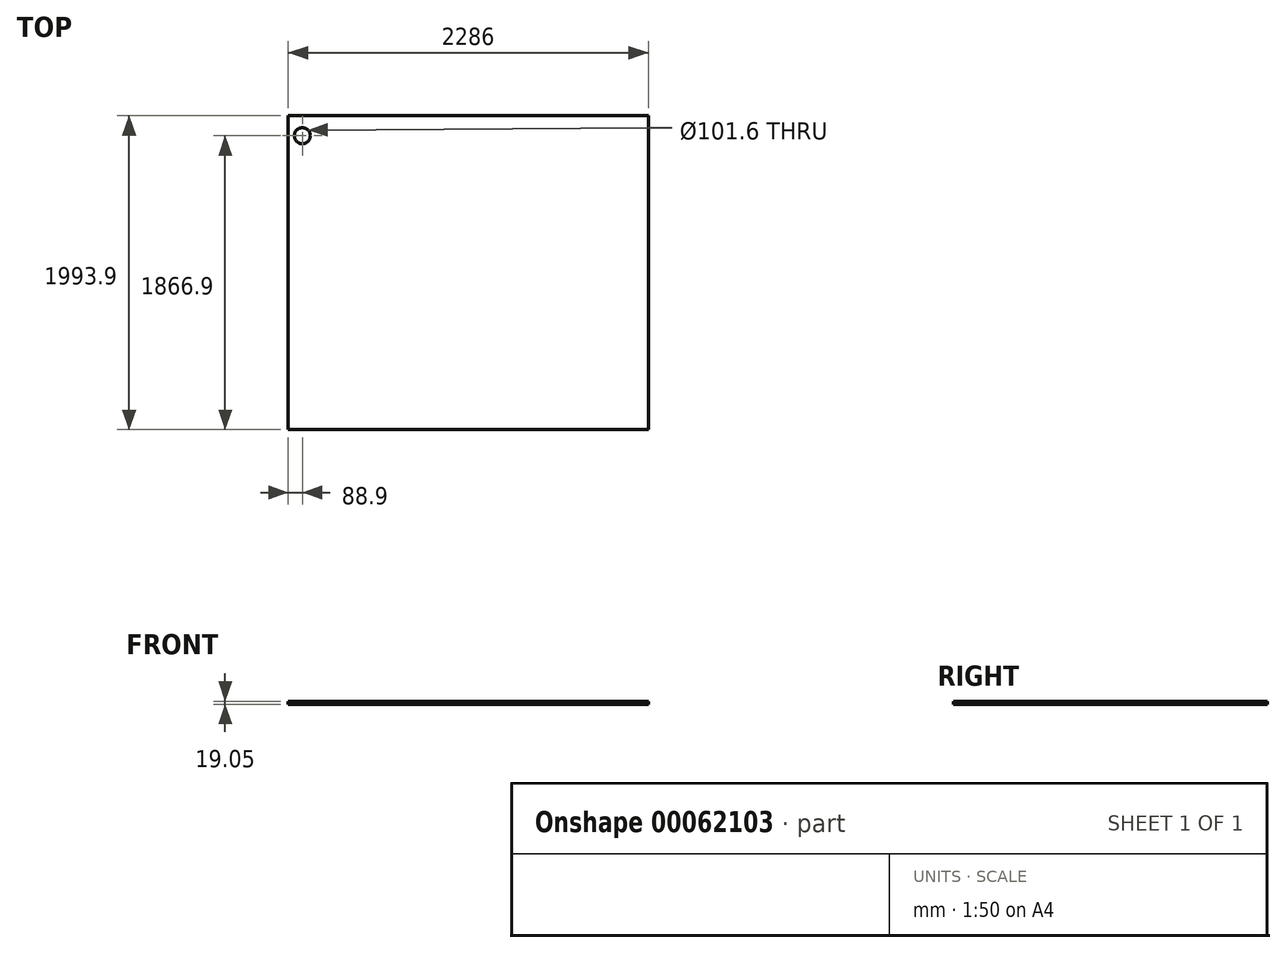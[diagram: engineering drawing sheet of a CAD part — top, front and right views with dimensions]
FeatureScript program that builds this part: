
annotation { "Feature Type Name" : "Feature", "Feature Type Description" : "" }
export const myFeature = defineFeature(function(context is Context, id is Id, definition is map)
    precondition{}
    {
        {
            var Q0;
            Q0=qCreatedBy(makeId("Top.planeOp"),FACE);
            var sketch = newSketch(context, id + "F0", { "sketchPlane" : qUnion([Q0])});
            skLineSegment(sketch, "E0", {"start": v(0, 0) * mm, "end": v(0, 985.96) * mm, "construction": true});
            skLineSegment(sketch, "E1", {"start": v(0, 0) * mm, "end": v(1088.04, 0) * mm, "construction": true});
            skLineSegment(sketch, "E2.bottom", {"start": v(-1143, 996.95) * mm, "end": v(1143, 996.95) * mm});
            skLineSegment(sketch, "E2.top", {"start": v(-1143, -996.95) * mm, "end": v(1143, -996.95) * mm});
            skLineSegment(sketch, "E2.left", {"start": v(-1143, 996.95) * mm, "end": v(-1143, -996.95) * mm});
            skLineSegment(sketch, "E2.right", {"start": v(1143, 996.95) * mm, "end": v(1143, -996.95) * mm});
            skSolve(sketch);
        }
        {
            var Q0;
            Q0=makeQuery(id+"F0.imprint","IMPRINT",FACE,{"disambiguationData":[TD([[makeQuery(id+"F0.imprint","IMPRINT",EDGE,{"derivedFrom":sQuery(id+"F0.wireOp",EDGE,"E2.bottom")}),-1.0]])]});
            extrude(context, id + "F1", {"entities" : qUnion([Q0]), "depth" : 19.05 * mm});
        }
        {
            var Q0;
            Q0=makeQuery(id+"F1.opExtrude","CAP_FACE",FACE,{"disambiguationData":[OSD([sQuery(id+"F0.wireOp",EDGE,"E2.bottom"),sQuery(id+"F0.wireOp",EDGE,"E2.top"),sQuery(id+"F0.wireOp",EDGE,"E2.left"),sQuery(id+"F0.wireOp",EDGE,"E2.right")])],"isStart":false});
            var sketch = newSketch(context, id + "F2", { "sketchPlane" : qUnion([Q0])});
            skCircle(sketch, "E3", {"center": v(-1054.1, 869.95) * mm, "radius": 50.8 * mm});
            skSolve(sketch);
        }
        {
            var Q0;
            Q0=makeQuery(id+"F2.imprint","IMPRINT",FACE,{"disambiguationData":[TD([[makeQuery(id+"F2.imprint","IMPRINT",EDGE,{"derivedFrom":sQuery(id+"F2.wireOp",EDGE,"E3")}),-1.0]])]});
            extrude(context, id + "F3", {"entities" : qUnion([Q0]), "operationType" : NewBodyOperationType.INTERSECT, "endBound" : BoundingType.THROUGH_ALL, "oppositeDirection" : true, "depth" : 25.4 * mm});
        }
    });
